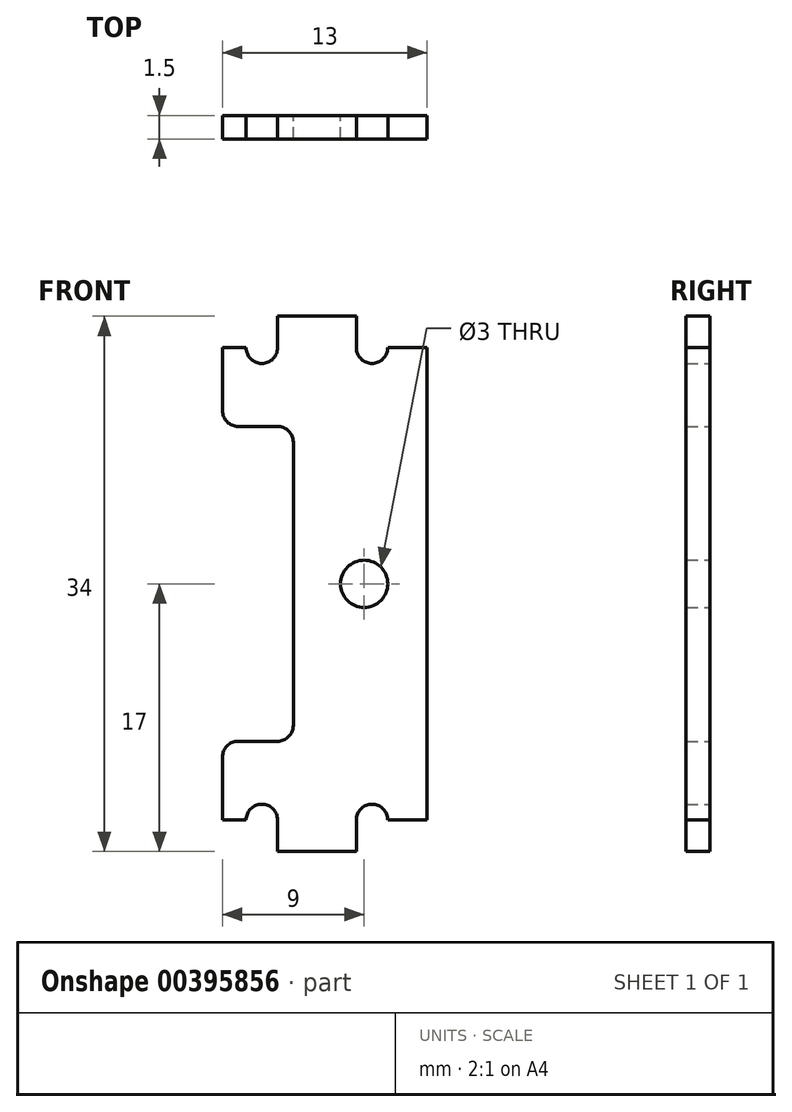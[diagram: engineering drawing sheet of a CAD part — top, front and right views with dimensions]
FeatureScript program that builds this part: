
annotation { "Feature Type Name" : "Feature", "Feature Type Description" : "" }
export const myFeature = defineFeature(function(context is Context, id is Id, definition is map)
    precondition{}
    {
        {
            var Q0;
            Q0=qCreatedBy(makeId("Front.planeOp"),FACE);
            var sketch = newSketch(context, id + "F0", { "sketchPlane" : qUnion([Q0])});
            skLineSegment(sketch, "E0.bottom", {"start": v(-6, 15) * mm, "end": v(-4.5, 15) * mm});
            skLineSegment(sketch, "E0.top", {"start": v(-6, -15) * mm, "end": v(-4.5, -15) * mm});
            skLineSegment(sketch, "E0.left", {"start": v(-6, 15) * mm, "end": v(-6, 11) * mm});
            skLineSegment(sketch, "E1.top", {"start": v(-2.5, 17) * mm, "end": v(2.5, 17) * mm});
            skLineSegment(sketch, "E1.left", {"start": v(-2.5, 15) * mm, "end": v(-2.5, 17) * mm});
            skLineSegment(sketch, "E1.right", {"start": v(2.5, 15) * mm, "end": v(2.5, 17) * mm});
            skArc(sketch, "E2", {"start": v(-4.5, 15) * mm, "mid": v(-3.5, 14) * mm, "end": v(-2.5, 15) * mm});
            skArc(sketch, "E3", {"start": v(2.5, 15) * mm, "mid": v(3.5, 14) * mm, "end": v(4.5, 15) * mm});
            skLineSegment(sketch, "E4.trimOffspring", {"start": v(4.5, 15) * mm, "end": v(7, 15) * mm});
            skArc(sketch, "E5.MirrorCS", {"start": v(-4.5, -15) * mm, "mid": v(-3.5, -14) * mm, "end": v(-2.5, -15) * mm});
            skLineSegment(sketch, "E6.MirrorCS", {"start": v(-2.5, -15) * mm, "end": v(-2.5, -17) * mm});
            skLineSegment(sketch, "E7.MirrorCS", {"start": v(-2.5, -17) * mm, "end": v(2.5, -17) * mm});
            skLineSegment(sketch, "E8.MirrorCS", {"start": v(2.5, -15) * mm, "end": v(2.5, -17) * mm});
            skArc(sketch, "E9.MirrorCS", {"start": v(2.5, -15) * mm, "mid": v(3.5, -14) * mm, "end": v(4.5, -15) * mm});
            skLineSegment(sketch, "E10.trimOffspring", {"start": v(4.5, -15) * mm, "end": v(7, -15) * mm});
            skCircle(sketch, "E11", {"center": v(3, 0) * mm, "radius": 1.5 * mm});
            skLineSegment(sketch, "E12.bottom", {"start": v(-5, 10) * mm, "end": v(-2.5, 10) * mm});
            skLineSegment(sketch, "E12.top", {"start": v(-5, -10) * mm, "end": v(-2.5, -10) * mm});
            skLineSegment(sketch, "E12.right", {"start": v(-1.5, 9) * mm, "end": v(-1.5, -9) * mm});
            skLineSegment(sketch, "E13.trimOffspring", {"start": v(-6, -11) * mm, "end": v(-6, -15) * mm});
            skLineSegment(sketch, "E14.trimOffspring", {"start": v(7, 15) * mm, "end": v(7, -15) * mm});
            skPoint(sketch, "E15.visualSharp", {"position": v(-1.5, 10) * mm});
            skArc(sketch, "E15.filletArc", {"start": v(-1.5, 9) * mm, "mid": v(-1.8, 9.7) * mm, "end": v(-2.5, 10) * mm});
            skPoint(sketch, "E16.visualSharp", {"position": v(-1.5, -10) * mm});
            skArc(sketch, "E16.filletArc", {"start": v(-2.5, -10) * mm, "mid": v(-1.8, -9.7) * mm, "end": v(-1.5, -9) * mm});
            skPoint(sketch, "E17.visualSharp", {"position": v(-6, -10) * mm});
            skArc(sketch, "E17.filletArc", {"start": v(-5, -10) * mm, "mid": v(-5.7, -10.3) * mm, "end": v(-6, -11) * mm});
            skPoint(sketch, "E18.visualSharp", {"position": v(-6, 10) * mm});
            skArc(sketch, "E18.filletArc", {"start": v(-6, 11) * mm, "mid": v(-5.7, 10.3) * mm, "end": v(-5, 10) * mm});
            skSolve(sketch);
        }
        {
            var Q0;
            Q0=qSketchRegion(id+"F0",true);
            extrude(context, id + "F1", {"entities" : qUnion([Q0]), "depth" : 1.5 * mm});
        }
    });
